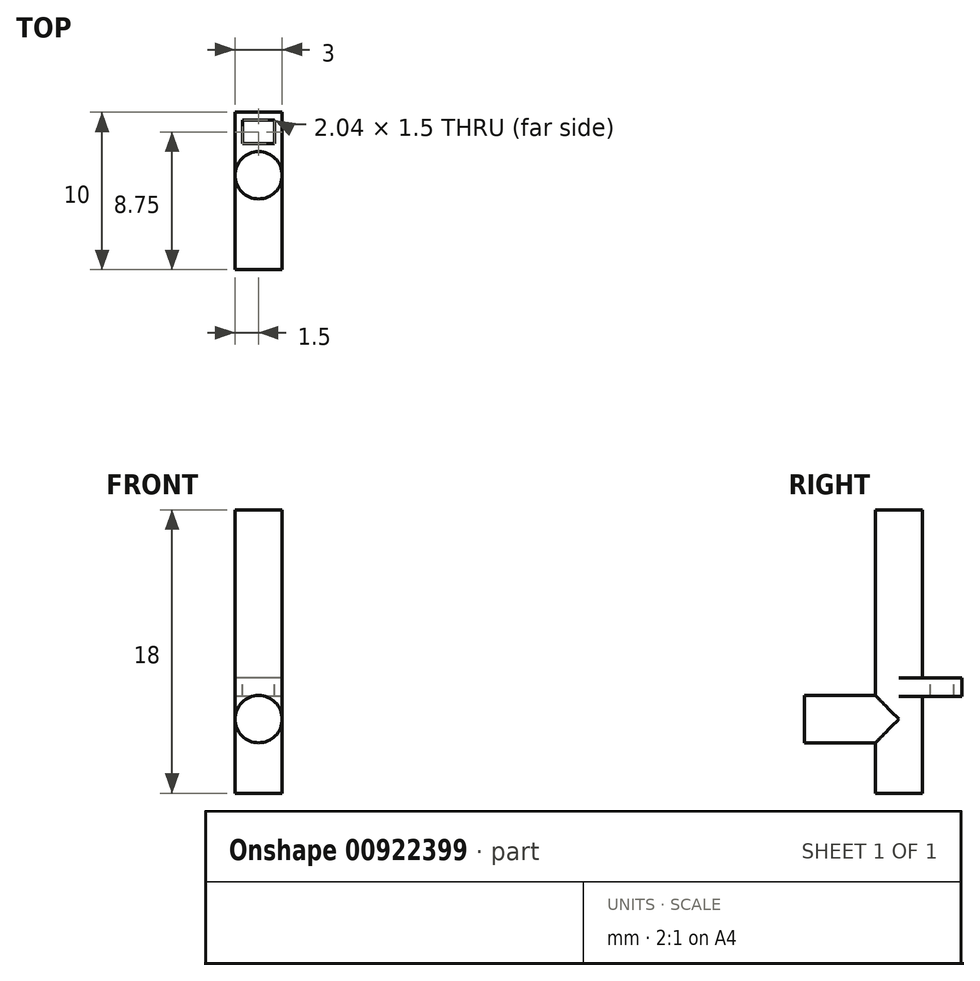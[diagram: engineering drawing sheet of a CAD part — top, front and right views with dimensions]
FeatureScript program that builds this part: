
annotation { "Feature Type Name" : "Feature", "Feature Type Description" : "" }
export const myFeature = defineFeature(function(context is Context, id is Id, definition is map)
    precondition{}
    {
        {
            var Q0;
            Q0=qCreatedBy(makeId("Top.planeOp"),FACE);
            var sketch = newSketch(context, id + "F0", { "sketchPlane" : qUnion([Q0])});
            skCircle(sketch, "E0", {"center": v(0, 0) * mm, "radius": 1.5 * mm});
            skSolve(sketch);
        }
        {
            var Q0;
            Q0=qSketchRegion(id+"F0",true);
            var Q1;
            Q1=makeQuery(id+"F0.imprint","IMPRINT",FACE,{"disambiguationData":[TD([[makeQuery(id+"F0.imprint","IMPRINT",EDGE,{"derivedFrom":sQuery(id+"F0.wireOp",EDGE,"E0")}),1.0]])]});
            extrude(context, id + "F1", {"entities" : qUnion([Q0, Q1]), "depth" : 18 * mm});
        }
        {
            var Q0;
            Q0=qCreatedBy(makeId("Front.planeOp"),FACE);
            var sketch = newSketch(context, id + "F2", { "sketchPlane" : qUnion([Q0])});
            skCircle(sketch, "E1", {"center": v(0, 4.7) * mm, "radius": 1.5 * mm});
            skSolve(sketch);
        }
        {
            var Q0;
            Q0=qSketchRegion(id+"F2",true);
            extrude(context, id + "F3", {"entities" : qUnion([Q0]), "operationType" : NewBodyOperationType.ADD, "depth" : 6 * mm});
        }
        {
            var Q0;
            Q0=qCreatedBy(makeId("Front.planeOp"),FACE);
            var sketch = newSketch(context, id + "F4", { "sketchPlane" : qUnion([Q0])});
            skLineSegment(sketch, "E2.bottom", {"start": v(1.5, 7.32) * mm, "end": v(-1.5, 7.32) * mm});
            skLineSegment(sketch, "E2.top", {"start": v(1.5, 6.16) * mm, "end": v(-1.5, 6.16) * mm});
            skLineSegment(sketch, "E2.left", {"start": v(1.5, 7.32) * mm, "end": v(1.5, 6.16) * mm});
            skLineSegment(sketch, "E2.right", {"start": v(-1.5, 7.32) * mm, "end": v(-1.5, 6.16) * mm});
            skPoint(sketch, "E2.middle", {"position": v(0, 6.74) * mm});
            skSolve(sketch);
        }
        {
            var Q0;
            Q0=qSketchRegion(id+"F4",true);
            extrude(context, id + "F5", {"entities" : qUnion([Q0]), "operationType" : NewBodyOperationType.ADD, "oppositeDirection" : true, "depth" : 4 * mm});
        }
        {
            var Q0;
            Q0=makeQuery(id+"F5.opExtrude","SWEPT_FACE",FACE,{"disambiguationData":[OSD([sQuery(id+"F4.wireOp",EDGE,"E2.bottom")])]});
            var sketch = newSketch(context, id + "F6", { "sketchPlane" : qUnion([Q0])});
            skLineSegment(sketch, "E3.bottom", {"start": v(1.02, 2) * mm, "end": v(-1.02, 2) * mm});
            skLineSegment(sketch, "E3.top", {"start": v(1.02, 3.5) * mm, "end": v(-1.02, 3.5) * mm});
            skLineSegment(sketch, "E3.left", {"start": v(1.02, 2) * mm, "end": v(1.02, 3.5) * mm});
            skLineSegment(sketch, "E3.right", {"start": v(-1.02, 2) * mm, "end": v(-1.02, 3.5) * mm});
            skPoint(sketch, "E3.middle", {"position": v(0, 2.75) * mm});
            skPoint(sketch, "E3.cornerSnap0", {"position": v(1.5, 2) * mm});
            skSolve(sketch);
        }
        {
            var Q0;
            Q0=qSketchRegion(id+"F6",true);
            extrude(context, id + "F7", {"entities" : qUnion([Q0]), "operationType" : NewBodyOperationType.REMOVE, "oppositeDirection" : true, "depth" : 25 * mm});
        }
    });
